# Revit family: Base_Cabinet-Danver-Trash_Base
name_source: partatom
category: Casework
units: mm (PartAtom-declared; Revit-internal decimal feet)

## family parameters
Always vertical = Yes
Classification Number = 23.40.35.17.47
Cut with Voids When Loaded = No
Room Calculation Point = No
Shared = No
Work Plane-Based = No

## types (1)
- Not a Type - Load Type Catalog
    Cabinet Material = Metal - Danver - Stainless Steel
    Construction Type = 304 Grade Stainless Steel
    Default Elevation = 0' - 0"
    Depth = 2' - 3"
    Depth+Door = 2' - 3 7/8"
    Description = Please Load Accompanying Type Catalog (.txt)
    Door Count = 1
    Door Style = Drawer : Hampton
    Drawer Count = 1
    Drawer Depth = 0' - 6 1/8"
    Handle Material = Metal - Danver - Chrome Plated Steel
    Height = 2' - 5 3/4"
    Keynote = 12 35 28
    Manufacturer = Danver Outdoor Kitchens
    Model = Please Load Accompanying Type Catalog (.txt)
    Product Documentation Link = https://danver.com
    Product Name = Base Cabinet - Trash Base
    Product Page URL = https://danver.com
    Toe Height = 0' - 4 1/2"
    Toe Kick Material = Metal - Danver - Toe Kick
    URL = www.danver.com
    V_Door = Yes
    V_Drawer = Yes
    Version = 2019 - V1.0b
    Width = 2' - 0"

## geometry (parser evidence)
native form markers: Sweep x23
no freeform markers — native parametric forms only
